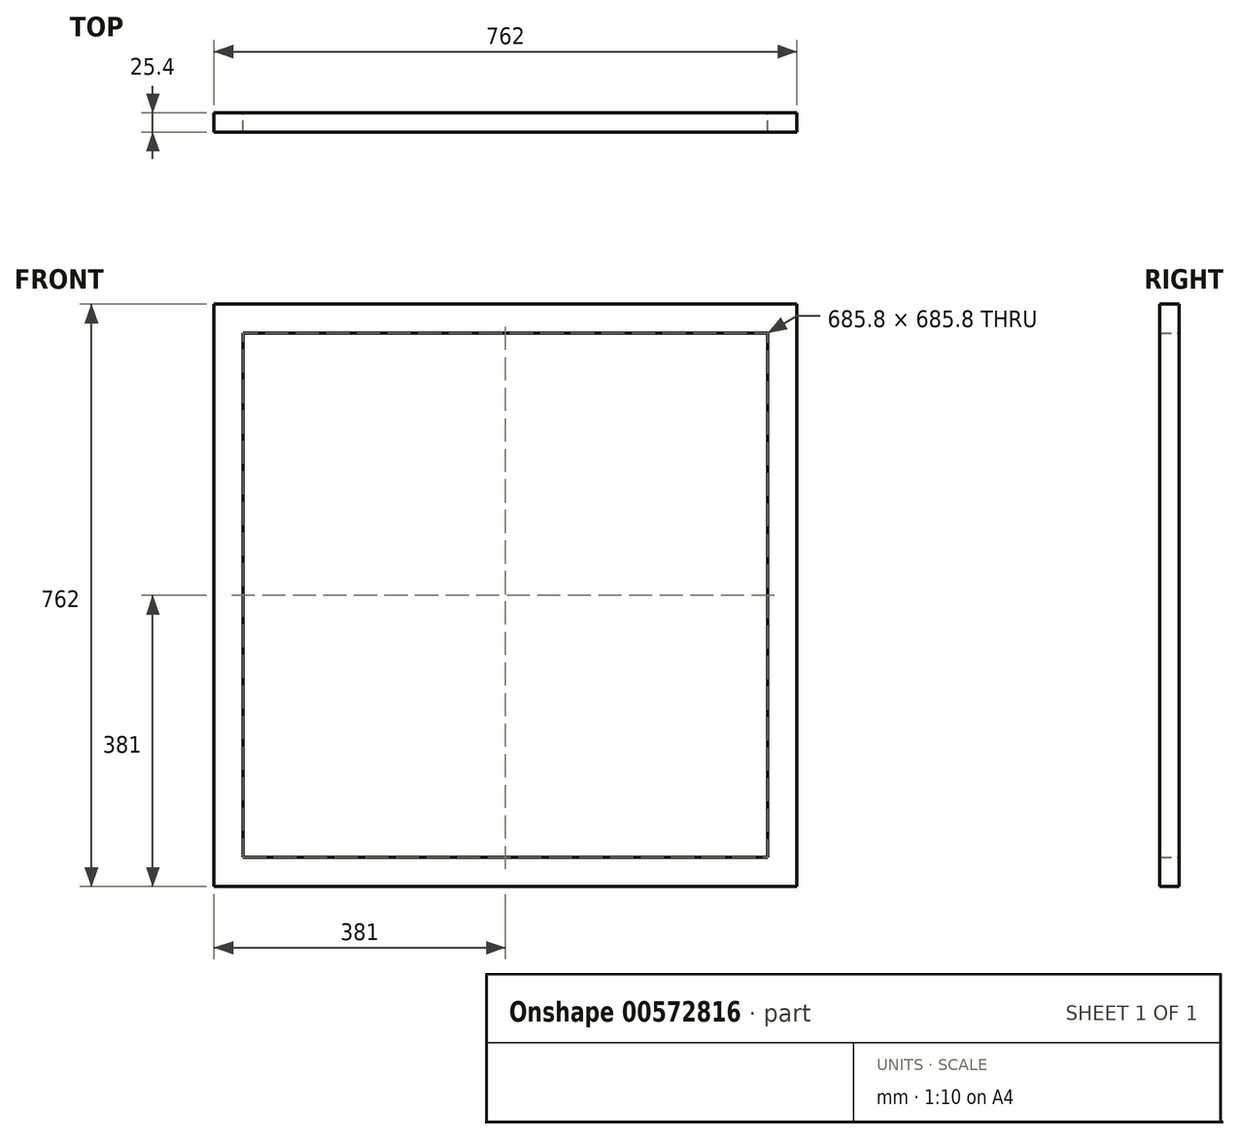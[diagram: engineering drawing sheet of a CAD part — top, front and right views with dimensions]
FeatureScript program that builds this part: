
annotation { "Feature Type Name" : "Feature", "Feature Type Description" : "" }
export const myFeature = defineFeature(function(context is Context, id is Id, definition is map)
    precondition{}
    {
        {
            var Q0;
            Q0=qCreatedBy(makeId("Front.planeOp"),FACE);
            var sketch = newSketch(context, id + "F0", { "sketchPlane" : qUnion([Q0])});
            skLineSegment(sketch, "E0.bottom", {"start": v(381, 381) * mm, "end": v(-381, 381) * mm});
            skLineSegment(sketch, "E0.top", {"start": v(381, -381) * mm, "end": v(-381, -381) * mm});
            skLineSegment(sketch, "E0.left", {"start": v(381, 381) * mm, "end": v(381, -381) * mm});
            skLineSegment(sketch, "E0.right", {"start": v(-381, 381) * mm, "end": v(-381, -381) * mm});
            skPoint(sketch, "E0.middle", {"position": v(0, 0) * mm});
            skLineSegment(sketch, "E1.bottom", {"start": v(342.9, 342.9) * mm, "end": v(-342.9, 342.9) * mm});
            skLineSegment(sketch, "E1.top", {"start": v(342.9, -342.9) * mm, "end": v(-342.9, -342.9) * mm});
            skLineSegment(sketch, "E1.left", {"start": v(342.9, 342.9) * mm, "end": v(342.9, -342.9) * mm});
            skLineSegment(sketch, "E1.right", {"start": v(-342.9, 342.9) * mm, "end": v(-342.9, -342.9) * mm});
            skSolve(sketch);
        }
        {
            var Q0;
            Q0=makeQuery(id+"F0.imprint","IMPRINT",FACE,{"disambiguationData":[TD([[makeQuery(id+"F0.imprint","IMPRINT",EDGE,{"derivedFrom":sQuery(id+"F0.wireOp",EDGE,"E0.bottom")}),1.0]])]});
            extrude(context, id + "F1", {"entities" : qUnion([Q0]), "depth" : 25.4 * mm, "offsetDistance" : 25.4 * mm});
        }
    });
